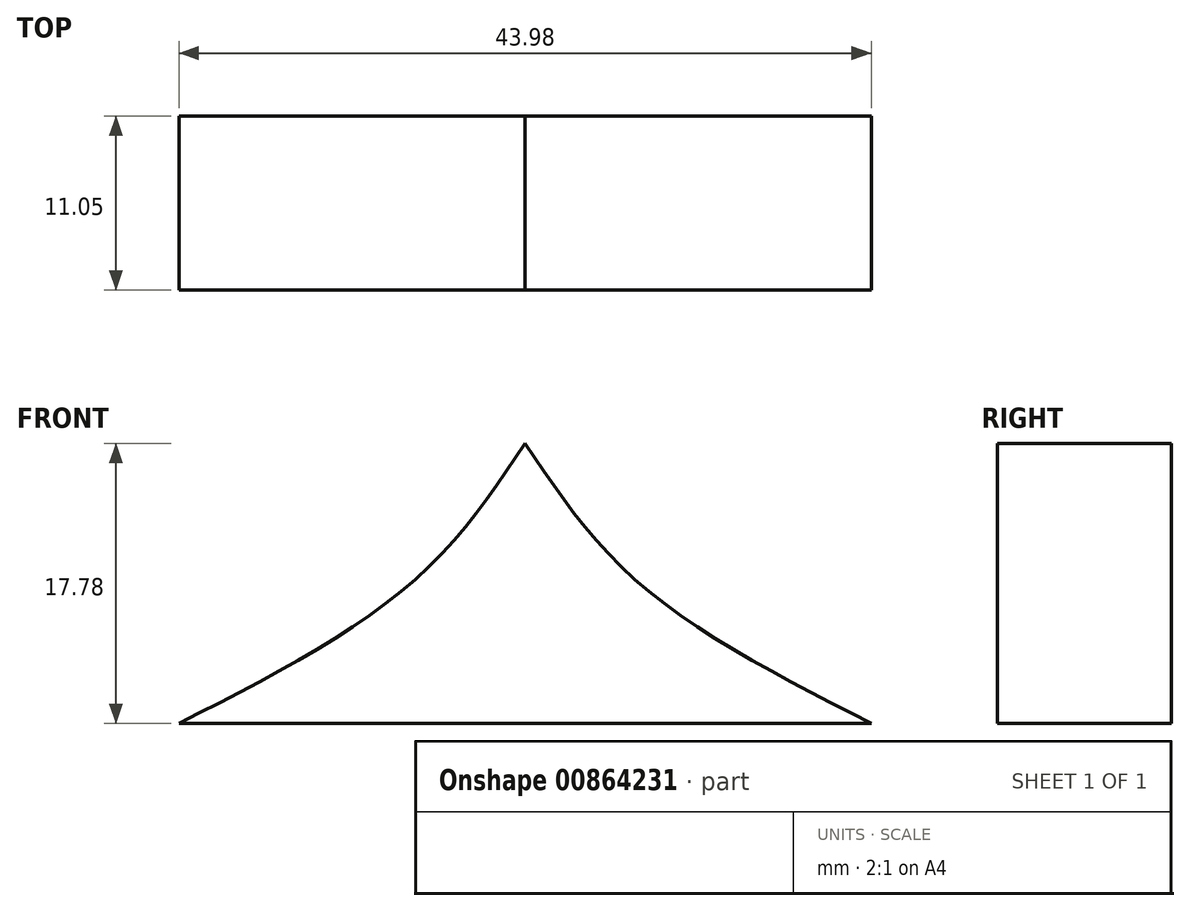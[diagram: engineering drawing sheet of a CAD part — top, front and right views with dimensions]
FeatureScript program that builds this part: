
annotation { "Feature Type Name" : "Feature", "Feature Type Description" : "" }
export const myFeature = defineFeature(function(context is Context, id is Id, definition is map)
    precondition{}
    {
        {
            var Q0;
            Q0=qCreatedBy(makeId("Front.planeOp"),FACE);
            var sketch = newSketch(context, id + "F0", { "sketchPlane" : qUnion([Q0])});
            skLineSegment(sketch, "E0", {"start": v(0, 0) * mm, "end": v(0, 17.78) * mm});
            skPoint(sketch, "E1.1.internal.snap0", {"position": v(0, 8.9) * mm});
            skFitSpline(sketch, "E1", {"points": [v(0, 17.78) * mm, v(-7.26, 8.9) * mm, v(-22, 0) * mm], "startDerivative": vector(-13.77, -20.59) * mm, "endDerivative": vector(-29.68, -15.15) * mm});
            skLineSegment(sketch, "E2", {"start": v(-22, 0) * mm, "end": v(0, 0) * mm});
            skLineSegment(sketch, "E3.MirrorCS", {"start": v(22, 0) * mm, "end": v(0, 0) * mm});
            skFitSpline(sketch, "E4.MirrorCS", {"points": [v(0, 17.78) * mm, v(7.26, 8.9) * mm, v(22, 0) * mm], "startDerivative": vector(13.77, -20.59) * mm, "endDerivative": vector(29.68, -15.15) * mm});
            skSolve(sketch);
        }
        {
            var Q0;
            Q0=makeQuery(id+"F0.imprint","IMPRINT",FACE,{"disambiguationData":[TD([[makeQuery(id+"F0.imprint","IMPRINT",EDGE,{"derivedFrom":sQuery(id+"F0.wireOp",EDGE,"E0")}),1.0]])]});
            var Q1;
            Q1=makeQuery(id+"F0.imprint","IMPRINT",FACE,{"disambiguationData":[TD([[makeQuery(id+"F0.imprint","IMPRINT",EDGE,{"derivedFrom":sQuery(id+"F0.wireOp",EDGE,"E0")}),-1.0]])]});
            extrude(context, id + "F1", {"entities" : qUnion([Q0, Q1]), "depth" : 11.05 * mm, "offsetDistance" : 25.4 * mm});
        }
    });
